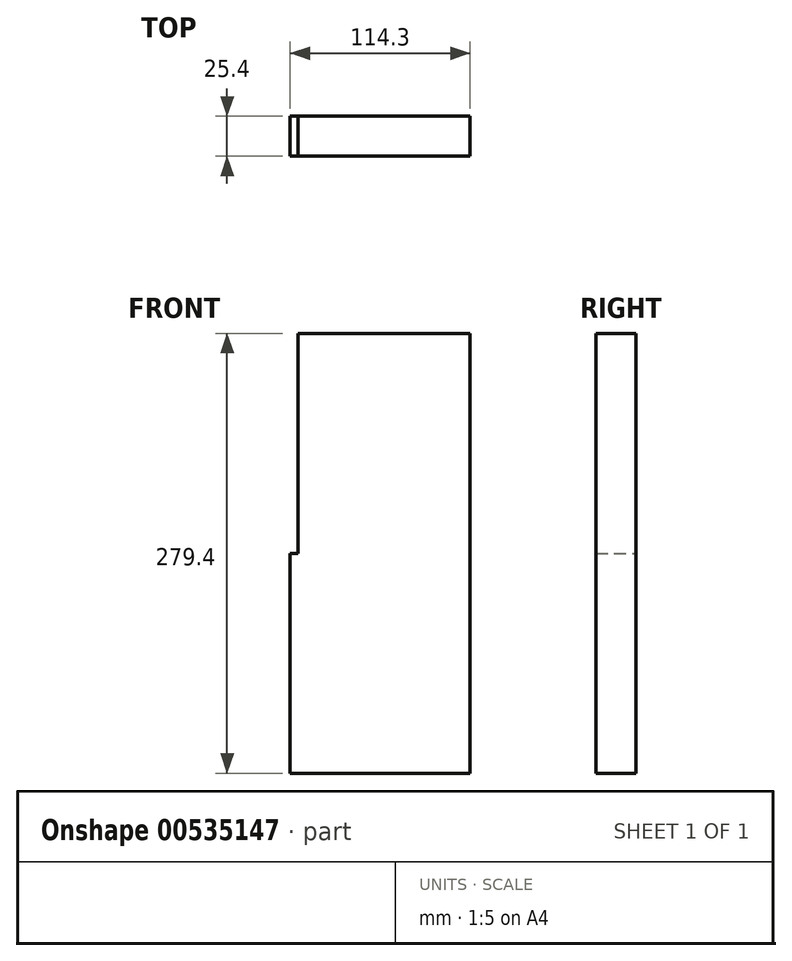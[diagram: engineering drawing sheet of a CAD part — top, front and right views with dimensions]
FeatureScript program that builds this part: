
annotation { "Feature Type Name" : "Feature", "Feature Type Description" : "" }
export const myFeature = defineFeature(function(context is Context, id is Id, definition is map)
    precondition{}
    {
        {
            var Q0;
            Q0=qCreatedBy(makeId("Front.planeOp"),FACE);
            var sketch = newSketch(context, id + "F0", { "sketchPlane" : qUnion([Q0])});
            skLineSegment(sketch, "E0.bottom", {"start": v(0, 0) * mm, "end": v(114.3, 0) * mm});
            skLineSegment(sketch, "E0.top", {"start": v(5.08, 279.4) * mm, "end": v(114.3, 279.4) * mm});
            skLineSegment(sketch, "E0.left", {"start": v(0, 0) * mm, "end": v(0, 139.7) * mm});
            skLineSegment(sketch, "E1.top", {"start": v(0, 139.7) * mm, "end": v(5.08, 139.7) * mm});
            skLineSegment(sketch, "E1.right", {"start": v(5.08, 279.4) * mm, "end": v(5.08, 139.7) * mm});
            skLineSegment(sketch, "E2", {"start": v(114.3, 279.4) * mm, "end": v(114.3, 0) * mm});
            skSolve(sketch);
        }
        {
            var Q0;
            Q0=qSketchRegion(id+"F0",true);
            extrude(context, id + "F1", {"entities" : qUnion([Q0]), "depth" : 25.4 * mm});
        }
    });
